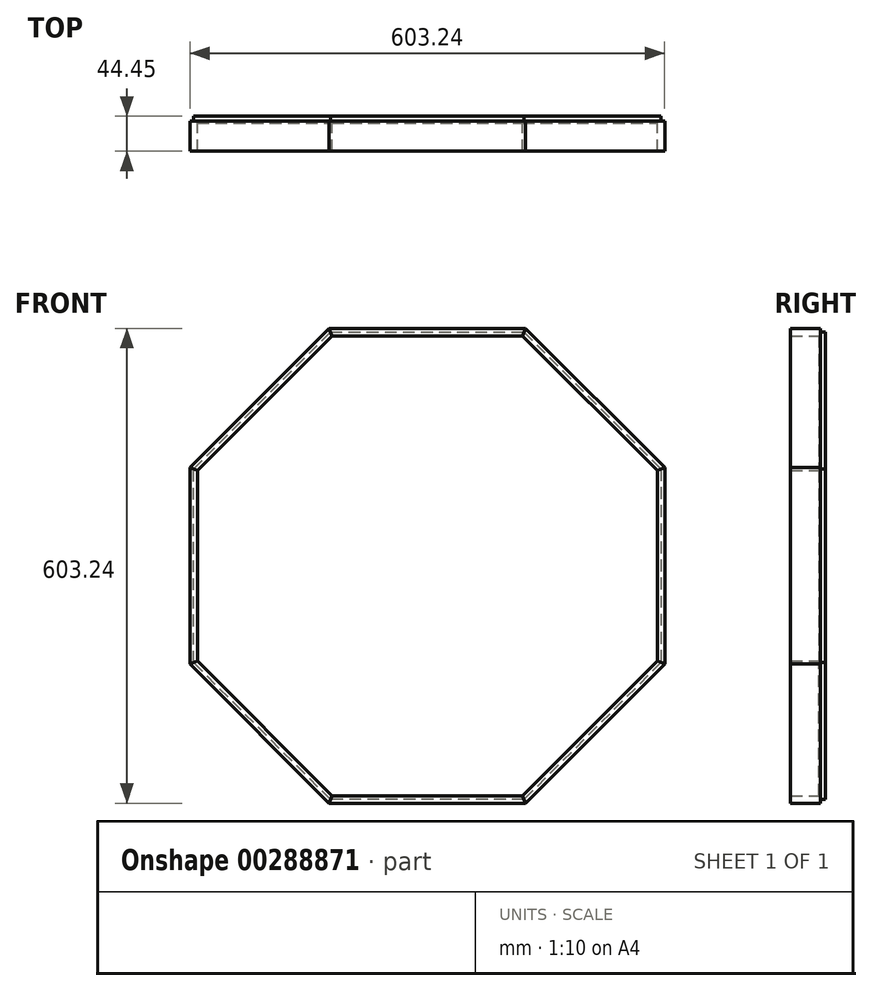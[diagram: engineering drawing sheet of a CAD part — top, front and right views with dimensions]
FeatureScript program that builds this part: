
annotation { "Feature Type Name" : "Feature", "Feature Type Description" : "" }
export const myFeature = defineFeature(function(context is Context, id is Id, definition is map)
    precondition{}
    {
        {
            assignVariable(context, id + "F0", {"name" : "foamT", "anyValue" : 2});
        }
        {
            var Q0;
            Q0=qCreatedBy(makeId("Front.planeOp"),FACE);
            var sketch = newSketch(context, id + "F1", { "sketchPlane" : qUnion([Q0])});
            skPoint(sketch, "E0.middle", {"position": v(0, 0) * mm});
            skCircle(sketch, "E1", {"center": v(0, 0) * mm, "radius": 316.17 * mm, "construction": true});
            skLineSegment(sketch, "E2.0", {"start": v(292.1, 121) * mm, "end": v(292.1, -121) * mm});
            skLineSegment(sketch, "E2.1", {"start": v(292.1, -121) * mm, "end": v(121, -292.1) * mm});
            skLineSegment(sketch, "E2.2", {"start": v(121, -292.1) * mm, "end": v(-121, -292.1) * mm});
            skLineSegment(sketch, "E2.3", {"start": v(-121, -292.1) * mm, "end": v(-292.1, -121) * mm});
            skLineSegment(sketch, "E2.4", {"start": v(-292.1, -121) * mm, "end": v(-292.1, 121) * mm});
            skLineSegment(sketch, "E2.5", {"start": v(-292.1, 121) * mm, "end": v(-121, 292.1) * mm});
            skLineSegment(sketch, "E2.6", {"start": v(-121, 292.1) * mm, "end": v(121, 292.1) * mm});
            skLineSegment(sketch, "E2.7", {"start": v(121, 292.1) * mm, "end": v(292.1, 121) * mm});
            skSolve(sketch);
        }
        {
            var Q0;
            Q0 = qSketchRegion(id + "F1", true);
            extrude(context, id + "F2", {"entities" : qUnion([Q0]), "depth" : (getVariable(context, 'foamT')) * mm});
        }
        {
            var Q0;
            Q0=makeQuery(id+"F2.opExtrude","CAP_FACE",FACE,{"disambiguationData":[OSD([sQuery(id+"F1.wireOp",EDGE,"E2.0"),sQuery(id+"F1.wireOp",EDGE,"E2.1"),sQuery(id+"F1.wireOp",EDGE,"E2.2"),sQuery(id+"F1.wireOp",EDGE,"E2.3"),sQuery(id+"F1.wireOp",EDGE,"E2.4"),sQuery(id+"F1.wireOp",EDGE,"E2.5"),sQuery(id+"F1.wireOp",EDGE,"E2.6"),sQuery(id+"F1.wireOp",EDGE,"E2.7")])],"isStart":true});
            var sketch = newSketch(context, id + "F3", { "sketchPlane" : qUnion([Q0])});
            skLineSegment(sketch, "E3.0", {"start": v(301.62, -124.94) * mm, "end": v(301.62, 124.94) * mm, "construction": true});
            skLineSegment(sketch, "E3.1", {"start": v(124.94, -301.62) * mm, "end": v(301.62, -124.94) * mm, "construction": true});
            skLineSegment(sketch, "E3.2", {"start": v(301.62, 124.94) * mm, "end": v(124.94, 301.62) * mm, "construction": true});
            skLineSegment(sketch, "E3.3", {"start": v(-124.94, -301.62) * mm, "end": v(124.94, -301.62) * mm, "construction": true});
            skLineSegment(sketch, "E3.4", {"start": v(124.94, 301.62) * mm, "end": v(-124.94, 301.62) * mm, "construction": true});
            skLineSegment(sketch, "E3.5", {"start": v(-124.94, 301.62) * mm, "end": v(-301.62, 124.94) * mm, "construction": true});
            skLineSegment(sketch, "E3.6", {"start": v(-301.62, 124.94) * mm, "end": v(-301.62, -124.94) * mm, "construction": true});
            skLineSegment(sketch, "E3.7", {"start": v(-301.62, -124.94) * mm, "end": v(-124.94, -301.62) * mm, "construction": true});
            skSolve(sketch);
        }
        {
            var Q0;
            Q0=qCreatedBy(makeId("Front.planeOp"),FACE);
            var sketch = newSketch(context, id + "F4", { "sketchPlane" : qUnion([Q0])});
            skLineSegment(sketch, "E4.0", {"start": v(-124.94, 301.62) * mm, "end": v(124.94, 301.62) * mm});
            skLineSegment(sketch, "E5.0", {"start": v(-121, 292.1) * mm, "end": v(121, 292.1) * mm});
            skLineSegment(sketch, "E6", {"start": v(-121, 292.1) * mm, "end": v(-124.94, 301.62) * mm});
            skLineSegment(sketch, "E7", {"start": v(121, 292.1) * mm, "end": v(124.94, 301.62) * mm});
            skSolve(sketch);
        }
        {
            var Q0;
            Q0 = qSketchRegion(id + "F4", true);
            extrude(context, id + "F5", {"entities" : qUnion([Q0]), "depth" : 38.1 * mm, "hasSecondDirection" : true, "secondDirectionOppositeDirection" : true, "secondDirectionDepth" : 1 / 101.6 * mm});
        }
        {
            var Q0;
            Q0=makeQuery(id+"F5.opExtrude","SWEPT_BODY",BODY,{"disambiguationData":[OSD([sQuery(id+"F4.wireOp",EDGE,"E4.0"),sQuery(id+"F4.wireOp",EDGE,"E5.0"),sQuery(id+"F4.wireOp",EDGE,"E6"),sQuery(id+"F4.wireOp",EDGE,"E7")])]});
            var Q1;
            Q1=qCreatedBy(makeId("Top.planeOp"),FACE);
            mirror(context, id + "F6", {"entities" : qUnion([Q0]), "mirrorPlane" : qUnion([Q1])});
        }
        {
            var Q0;
            Q0=makeQuery(id+"F5.opExtrude","SWEPT_BODY",BODY,{"disambiguationData":[OSD([sQuery(id+"F4.wireOp",EDGE,"E4.0"),sQuery(id+"F4.wireOp",EDGE,"E5.0"),sQuery(id+"F4.wireOp",EDGE,"E6"),sQuery(id+"F4.wireOp",EDGE,"E7")])]});
            var Q1;
            Q1=makeQuery(id+"F5.opExtrude","SWEPT_FACE",FACE,{"disambiguationData":[OSD([sQuery(id+"F4.wireOp",EDGE,"E7")])]});
            mirror(context, id + "F7", {"entities" : qUnion([Q0]), "mirrorPlane" : qUnion([Q1])});
        }
        {
            var Q0;
            Q0=makeQuery(id+"F7.opPattern","COPY",BODY,{"derivedFrom":makeQuery(id+"F5.opExtrude","SWEPT_BODY",BODY,{"disambiguationData":[OSD([sQuery(id+"F4.wireOp",EDGE,"E4.0"),sQuery(id+"F4.wireOp",EDGE,"E5.0"),sQuery(id+"F4.wireOp",EDGE,"E6"),sQuery(id+"F4.wireOp",EDGE,"E7")])]}),"instanceName":"1"});
            var Q1;
            Q1=makeQuery(id+"F7.opPattern","COPY",FACE,{"derivedFrom":makeQuery(id+"F5.opExtrude","SWEPT_FACE",FACE,{"disambiguationData":[OSD([sQuery(id+"F4.wireOp",EDGE,"E6")])]}),"instanceName":"1"});
            mirror(context, id + "F8", {"entities" : qUnion([Q0]), "mirrorPlane" : qUnion([Q1])});
        }
        {
            var Q0;
            Q0=makeQuery(id+"F8.opPattern","COPY",BODY,{"derivedFrom":makeQuery(id+"F7.opPattern","COPY",BODY,{"derivedFrom":makeQuery(id+"F5.opExtrude","SWEPT_BODY",BODY,{"disambiguationData":[OSD([sQuery(id+"F4.wireOp",EDGE,"E4.0"),sQuery(id+"F4.wireOp",EDGE,"E5.0"),sQuery(id+"F4.wireOp",EDGE,"E6"),sQuery(id+"F4.wireOp",EDGE,"E7")])]}),"instanceName":"1"}),"instanceName":"1"});
            var Q1;
            Q1=makeQuery(id+"F8.opPattern","COPY",FACE,{"derivedFrom":makeQuery(id+"F7.opPattern","COPY",FACE,{"derivedFrom":makeQuery(id+"F5.opExtrude","SWEPT_FACE",FACE,{"disambiguationData":[OSD([sQuery(id+"F4.wireOp",EDGE,"E7")])]}),"instanceName":"1"}),"instanceName":"1"});
            mirror(context, id + "F9", {"entities" : qUnion([Q0]), "mirrorPlane" : qUnion([Q1])});
        }
        {
            var Q0;
            Q0=makeQuery(id+"F6.opPattern","COPY",BODY,{"derivedFrom":makeQuery(id+"F5.opExtrude","SWEPT_BODY",BODY,{"disambiguationData":[OSD([sQuery(id+"F4.wireOp",EDGE,"E4.0"),sQuery(id+"F4.wireOp",EDGE,"E5.0"),sQuery(id+"F4.wireOp",EDGE,"E6"),sQuery(id+"F4.wireOp",EDGE,"E7")])]}),"instanceName":"1"});
            var Q1;
            Q1=makeQuery(id+"F6.opPattern","COPY",FACE,{"derivedFrom":makeQuery(id+"F5.opExtrude","SWEPT_FACE",FACE,{"disambiguationData":[OSD([sQuery(id+"F4.wireOp",EDGE,"E6")])]}),"instanceName":"1"});
            mirror(context, id + "F10", {"entities" : qUnion([Q0]), "mirrorPlane" : qUnion([Q1])});
        }
        {
            var Q0;
            Q0=makeQuery(id+"F10.opPattern","COPY",BODY,{"derivedFrom":makeQuery(id+"F6.opPattern","COPY",BODY,{"derivedFrom":makeQuery(id+"F5.opExtrude","SWEPT_BODY",BODY,{"disambiguationData":[OSD([sQuery(id+"F4.wireOp",EDGE,"E4.0"),sQuery(id+"F4.wireOp",EDGE,"E5.0"),sQuery(id+"F4.wireOp",EDGE,"E6"),sQuery(id+"F4.wireOp",EDGE,"E7")])]}),"instanceName":"1"}),"instanceName":"1"});
            var Q1;
            Q1=makeQuery(id+"F10.opPattern","COPY",FACE,{"derivedFrom":makeQuery(id+"F6.opPattern","COPY",FACE,{"derivedFrom":makeQuery(id+"F5.opExtrude","SWEPT_FACE",FACE,{"disambiguationData":[OSD([sQuery(id+"F4.wireOp",EDGE,"E7")])]}),"instanceName":"1"}),"instanceName":"1"});
            mirror(context, id + "F11", {"entities" : qUnion([Q0]), "mirrorPlane" : qUnion([Q1])});
        }
        {
            var Q0;
            Q0=makeQuery(id+"F11.opPattern","COPY",BODY,{"derivedFrom":makeQuery(id+"F10.opPattern","COPY",BODY,{"derivedFrom":makeQuery(id+"F6.opPattern","COPY",BODY,{"derivedFrom":makeQuery(id+"F5.opExtrude","SWEPT_BODY",BODY,{"disambiguationData":[OSD([sQuery(id+"F4.wireOp",EDGE,"E4.0"),sQuery(id+"F4.wireOp",EDGE,"E5.0"),sQuery(id+"F4.wireOp",EDGE,"E6"),sQuery(id+"F4.wireOp",EDGE,"E7")])]}),"instanceName":"1"}),"instanceName":"1"}),"instanceName":"1"});
            var Q1;
            Q1=makeQuery(id+"F11.opPattern","COPY",FACE,{"derivedFrom":makeQuery(id+"F10.opPattern","COPY",FACE,{"derivedFrom":makeQuery(id+"F6.opPattern","COPY",FACE,{"derivedFrom":makeQuery(id+"F5.opExtrude","SWEPT_FACE",FACE,{"disambiguationData":[OSD([sQuery(id+"F4.wireOp",EDGE,"E6")])]}),"instanceName":"1"}),"instanceName":"1"}),"instanceName":"1"});
            mirror(context, id + "F12", {"entities" : qUnion([Q0]), "mirrorPlane" : qUnion([Q1])});
        }
        {
            var Q0;
            Q0=makeQuery(id+"F3.imprint","IMPRINT",FACE,{"disambiguationData":[TD([[makeQuery(id+"F3.imprint","IMPRINT",EDGE,{"derivedFrom":makeQuery(id+"F2.opExtrude","CAP_EDGE",EDGE,{"disambiguationData":[OSD([sQuery(id+"F1.wireOp",EDGE,"E2.0")])],"isStart":true})}),1.0]])]});
            var sketch = newSketch(context, id + "F13", { "sketchPlane" : qUnion([Q0])});
            skLineSegment(sketch, "E8.0", {"start": v(122.96, -296.86) * mm, "end": v(296.86, -122.96) * mm});
            skLineSegment(sketch, "E8.1", {"start": v(-122.96, -296.86) * mm, "end": v(122.96, -296.86) * mm});
            skLineSegment(sketch, "E8.2", {"start": v(296.86, -122.96) * mm, "end": v(296.86, 122.96) * mm});
            skLineSegment(sketch, "E8.3", {"start": v(-296.86, -122.96) * mm, "end": v(-122.96, -296.86) * mm});
            skLineSegment(sketch, "E8.4", {"start": v(296.86, 122.96) * mm, "end": v(122.96, 296.86) * mm});
            skLineSegment(sketch, "E8.5", {"start": v(122.96, 296.86) * mm, "end": v(-122.96, 296.86) * mm});
            skLineSegment(sketch, "E8.6", {"start": v(-122.96, 296.86) * mm, "end": v(-296.86, 122.96) * mm});
            skLineSegment(sketch, "E8.7", {"start": v(-296.86, 122.96) * mm, "end": v(-296.86, -122.96) * mm});
            skSolve(sketch);
        }
        {
            var Q0;
            Q0 = qSketchRegion(id + "F13", true);
            extrude(context, id + "F14", {"entities" : qUnion([Q0]), "depth" : 6.35 * mm});
        }
        {
            var Q0;
            Q0=makeQuery(id+"F14.opExtrude","SWEPT_BODY",BODY,{"disambiguationData":[OSD([sQuery(id+"F13.wireOp",EDGE,"E8.0"),sQuery(id+"F13.wireOp",EDGE,"E8.1"),sQuery(id+"F13.wireOp",EDGE,"E8.2"),sQuery(id+"F13.wireOp",EDGE,"E8.3"),sQuery(id+"F13.wireOp",EDGE,"E8.4"),sQuery(id+"F13.wireOp",EDGE,"E8.5"),sQuery(id+"F13.wireOp",EDGE,"E8.6"),sQuery(id+"F13.wireOp",EDGE,"E8.7")])]});
            var Q1;
            Q1=makeQuery(id+"F5.opExtrude","SWEPT_BODY",BODY,{"disambiguationData":[OSD([sQuery(id+"F4.wireOp",EDGE,"E4.0"),sQuery(id+"F4.wireOp",EDGE,"E5.0"),sQuery(id+"F4.wireOp",EDGE,"E6"),sQuery(id+"F4.wireOp",EDGE,"E7")])]});
            var Q2;
            Q2=makeQuery(id+"F6.opPattern","COPY",BODY,{"derivedFrom":makeQuery(id+"F5.opExtrude","SWEPT_BODY",BODY,{"disambiguationData":[OSD([sQuery(id+"F4.wireOp",EDGE,"E4.0"),sQuery(id+"F4.wireOp",EDGE,"E5.0"),sQuery(id+"F4.wireOp",EDGE,"E6"),sQuery(id+"F4.wireOp",EDGE,"E7")])]}),"instanceName":"1"});
            var Q3;
            Q3=makeQuery(id+"F7.opPattern","COPY",BODY,{"derivedFrom":makeQuery(id+"F5.opExtrude","SWEPT_BODY",BODY,{"disambiguationData":[OSD([sQuery(id+"F4.wireOp",EDGE,"E4.0"),sQuery(id+"F4.wireOp",EDGE,"E5.0"),sQuery(id+"F4.wireOp",EDGE,"E6"),sQuery(id+"F4.wireOp",EDGE,"E7")])]}),"instanceName":"1"});
            var Q4;
            Q4=makeQuery(id+"F8.opPattern","COPY",BODY,{"derivedFrom":makeQuery(id+"F7.opPattern","COPY",BODY,{"derivedFrom":makeQuery(id+"F5.opExtrude","SWEPT_BODY",BODY,{"disambiguationData":[OSD([sQuery(id+"F4.wireOp",EDGE,"E4.0"),sQuery(id+"F4.wireOp",EDGE,"E5.0"),sQuery(id+"F4.wireOp",EDGE,"E6"),sQuery(id+"F4.wireOp",EDGE,"E7")])]}),"instanceName":"1"}),"instanceName":"1"});
            var Q5;
            Q5=makeQuery(id+"F9.opPattern","COPY",BODY,{"derivedFrom":makeQuery(id+"F8.opPattern","COPY",BODY,{"derivedFrom":makeQuery(id+"F7.opPattern","COPY",BODY,{"derivedFrom":makeQuery(id+"F5.opExtrude","SWEPT_BODY",BODY,{"disambiguationData":[OSD([sQuery(id+"F4.wireOp",EDGE,"E4.0"),sQuery(id+"F4.wireOp",EDGE,"E5.0"),sQuery(id+"F4.wireOp",EDGE,"E6"),sQuery(id+"F4.wireOp",EDGE,"E7")])]}),"instanceName":"1"}),"instanceName":"1"}),"instanceName":"1"});
            var Q6;
            Q6=makeQuery(id+"F10.opPattern","COPY",BODY,{"derivedFrom":makeQuery(id+"F6.opPattern","COPY",BODY,{"derivedFrom":makeQuery(id+"F5.opExtrude","SWEPT_BODY",BODY,{"disambiguationData":[OSD([sQuery(id+"F4.wireOp",EDGE,"E4.0"),sQuery(id+"F4.wireOp",EDGE,"E5.0"),sQuery(id+"F4.wireOp",EDGE,"E6"),sQuery(id+"F4.wireOp",EDGE,"E7")])]}),"instanceName":"1"}),"instanceName":"1"});
            var Q7;
            Q7=makeQuery(id+"F11.opPattern","COPY",BODY,{"derivedFrom":makeQuery(id+"F10.opPattern","COPY",BODY,{"derivedFrom":makeQuery(id+"F6.opPattern","COPY",BODY,{"derivedFrom":makeQuery(id+"F5.opExtrude","SWEPT_BODY",BODY,{"disambiguationData":[OSD([sQuery(id+"F4.wireOp",EDGE,"E4.0"),sQuery(id+"F4.wireOp",EDGE,"E5.0"),sQuery(id+"F4.wireOp",EDGE,"E6"),sQuery(id+"F4.wireOp",EDGE,"E7")])]}),"instanceName":"1"}),"instanceName":"1"}),"instanceName":"1"});
            var Q8;
            Q8=makeQuery(id+"F12.opPattern","COPY",BODY,{"derivedFrom":makeQuery(id+"F11.opPattern","COPY",BODY,{"derivedFrom":makeQuery(id+"F10.opPattern","COPY",BODY,{"derivedFrom":makeQuery(id+"F6.opPattern","COPY",BODY,{"derivedFrom":makeQuery(id+"F5.opExtrude","SWEPT_BODY",BODY,{"disambiguationData":[OSD([sQuery(id+"F4.wireOp",EDGE,"E4.0"),sQuery(id+"F4.wireOp",EDGE,"E5.0"),sQuery(id+"F4.wireOp",EDGE,"E6"),sQuery(id+"F4.wireOp",EDGE,"E7")])]}),"instanceName":"1"}),"instanceName":"1"}),"instanceName":"1"}),"instanceName":"1"});
            booleanBodies(context, id + "F15", {"operationType" : BooleanOperationType.SUBTRACTION, "tools" : qUnion([Q0]), "targets" : qUnion([Q1, Q2, Q3, Q4, Q5, Q6, Q7, Q8]), "keepTools" : true});
        }
    });
